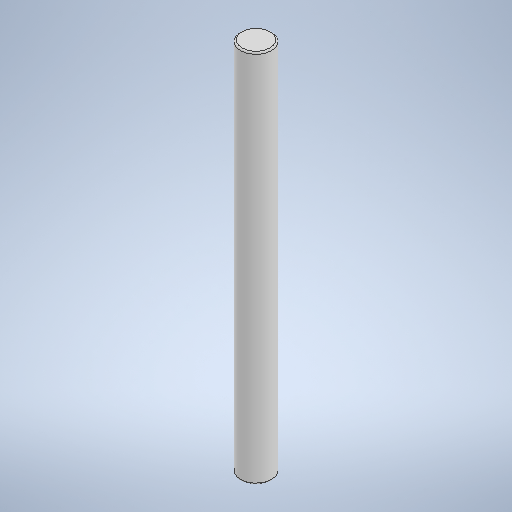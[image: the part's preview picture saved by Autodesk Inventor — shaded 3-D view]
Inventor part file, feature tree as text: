
AUTODESK INVENTOR PART (.ipt)
format: ipt  version: 2025.1 (Build 291241000, 241)  size: 253,440 bytes
history: native  units: mm
features: extrude x1, fillet x1, sketch x1
ambient origin geometry x8: Origin, YZ Plane, XZ Plane, XY Plane, X Axis, Y Axis, Z Axis, Center Point
bodies: Solid1 (feature_tree)
feature tree (3):
  extrude  "Extrusion1"  Depth=120.0mm TaperAngle=0.0deg
  fillet  "Fillet1"  Radius=0.5mm
  sketch  "Sketch1"  dims[d0=10.0mm d1=120.0mm d2=0.0mm d3=0.5mm]
